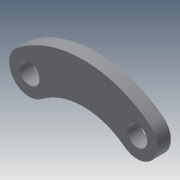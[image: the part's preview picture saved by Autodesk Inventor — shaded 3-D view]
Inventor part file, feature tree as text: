
AUTODESK INVENTOR PART (.ipt)
format: ipt  version: 2015 (Build 190159000, 159)  size: 92,160 bytes
history: native  units: mm
features: extrude x1, sketch x1
ambient origin geometry x8: Origin, YZ Plane, XZ Plane, XY Plane, X Axis, Y Axis, Z Axis, Center Point
bodies: Solid1 (feature_tree)
feature tree (2):
  extrude  "Extrusion1"  Depth=2.0mm
  sketch  "Sketch1"  dims[d13=16.0mm d14=6.0mm d16=6.0mm d17=3.0mm d18=3.0mm d19=2.0mm d20=0.0mm]
